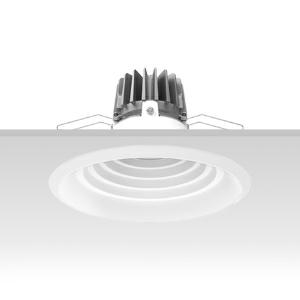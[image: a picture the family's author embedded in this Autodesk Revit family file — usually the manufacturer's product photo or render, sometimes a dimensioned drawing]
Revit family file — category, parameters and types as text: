
# Revit family: 3f_filippi_-_3f_reno_bianco_ellittico_3f_filippi_-_30789_-_3f_reno_200_wh_2000-930_ell
name_source: partatom
category: Lighting Fixtures
units: mm (PartAtom-declared; Revit-internal decimal feet)

## family parameters
Cut with Voids When Loaded = No
Host = Face
Light Source = No
Part Type = Normal
Room Calculation Point = No
Round Connector Dimension = Use Diameter
Shared = No

## types (1)
- 3F Filippi - 3F Reno Bianco Ellittico (1 x LED, 2005 lm, 24 W, 3000 K)
    Apparent Load = 24 VA
    Approval mark = CE
    CIE Flux Codes = 77 98 100 100 100
    Color Rendering = 90
    Color Temperature = 3000 K
    Control Gear = Electronic ballast
    Default Elevation = 1800 mm
    Description = ILLUMINOTECHNICAL
Luminous efficiency 100% (DLOR 100%, ULOR 0%).
Initial luminous flux of the luminaire 2005 lm.
Direct symmetric elliptical distribution.
Installation Interdistance Transv.D = 0.79 x hu - Long.D = 1.49 x hu.
Tabular UGR (CIE 117 - 4H-8H; S=0.25H; 70/50/20): RUG 17.1 - 21.6.
Beam angle: 65° - 93°.
Luminous efficacy 84 lm/W.
Lifetime (L90/B10): 30000 h. (tq+25°C)
Lifetime (L85/B10): 50000 h. (tq+25°C)
Lifetime (L70/B10): 80000 h. (tq+25°C)
Sudden decreased luminous flux after 50000 hours: 0% (C0).
Photobiological safety in compliance with IEC/TR 62778: RG1 low risk, (IEC 62471).
In compliance with IEC/EN 62722-2-1 - IEC/EN 62717 standards.

SOURCE
Compact LED module 2000/930.
Energy efficiency class (UE 2019/2020 - UE 2019/2015): E.
CIE 13.3 Colour rendering index: CRI >90 (R9 >50%).
IES TM-30 Fidelity Index: Rf = 92 Rg = 101.
CCT nominal colour temperature 3000 K.
Colour initial tolerance (MacAdam): SDCM 3.
Zhaga Book 3 compliant.

MECHANICAL
Passive heat dissipator in die-casting aluminium, oversized, for optimum thermal management of the LED module.
Parabolic element with graduated/concentric rings in white polycarbonate.
Internal specular metallic louvre to optimise control of the luminous flux in polycarbonate.
Transparent external lens with glossy and satin differentiated surfaces, with a cooling and anti-insect system in methacrylate (PMMA).
Fastening spring clips in stainless steel.
Dimensions: diameter 216 mm, height 142 mm. Weight 0.8 kg.
IP44 protection degree for exposed part, IP20 for recessed part.
Mechanical strength to impacts IK04 (0.5 joule).
Glow-wire test resistance 650°C.

ELECTRICAL
Wiring on a separate unit.
Halogen Free electronic wiring 230V-50/60Hz, power factor 0.95, THD <25%, constant output current, SELV, class II, 1 driver.
Power of the luminaire 24 W.
ENEC - CE.
SAFE FLICKER: PstLM=<1 and SVM=<0.4 (IEC TR 61547-1 and IEC TR 63158), to ensure a more comfortable and safe light.
Luminaire compliant with EN 60598-2-22 for power supply from a centralised emergency system CPSS (Central Power Supply System), not incorporated in the luminaire - high risk areas excluded. The default power and flux are 100% in AC and 100% in DC.
Ambient temperature from 0°C to +25°C.
Temperature class T6 max 85°C.
Relative humidity UR: <85%.

INSTALLATION
Pull-up recessed fitting.
False ceiling carving: 200 mm.
All accessories dedicated to this product are available on the Catalog and on our website www.3F-Filippi.com.

APPLICATIONS
Environments: architectural, commercial, exhibition areas, transit areas, corridors, shops, display windows, service areas.
In false ceilings with narrow voids.

WARNING
Luminaire designed for disposal/recycling at end-of-life.
Replaceable (LED only) light source by a professional. Replaceable control gear by a professional.
    Height = 0 mm  [stored 0 ft]
    Lamp = 1 x LED
    Lamp Light Flux = 2005 lm
    Lamp Power = 24 W
    Lamp count = 1
    Length = 216 mm
    Lifetime = 50000 h
    Luminous efficacy = 84 lm/W
    Manufacturer = 3F Filippi
    ModVariant = No
    Model = 3F Filippi - 30789 - 3F Reno 200 WH 2000-930 ELL
    Mounting Place = Ceiling
    Mounting Type = Recessed
    Number of Poles = 1
    OnlyDefault = Yes
    Power Factor = 1
    Product Name = 3F Filippi - 3F Reno Bianco Ellittico
    Product group = recessed luminaire
    ProductGroupID = 4
    Protection Class = Protection class II
    Protection Degree = IP 20
    RLX_Detail_Level = 1
    RLX_Emergency_Light_Flux = 0 lm
    RLX_Emergency_Type = 0
    RLX_Emergency_Type_DB = No
    RlxData = <blob elided: 89281 chars, md5=7f6fcb00>
    Socket = socket
    Standby Power = 0 W
    System Light Flux = 2005 lm
    System Power = 24 W
    Type Comments = Product without accessories
    Type Image = 3ffilippi_3f_reno_200_wh_2000.jpg
    URL = http://relux.com
    VarID = ---
    Voltage = 0 V
    Weight = 0.00 kg
    Width = 0 mm  [stored 0 ft]

note: [stored X ft] marks values corroborated as IEEE doubles in the binary element streams (Revit-internal decimal feet)

## geometry (parser evidence)
native form markers: Blend x4, Sweep x11
no freeform markers — native parametric forms only
